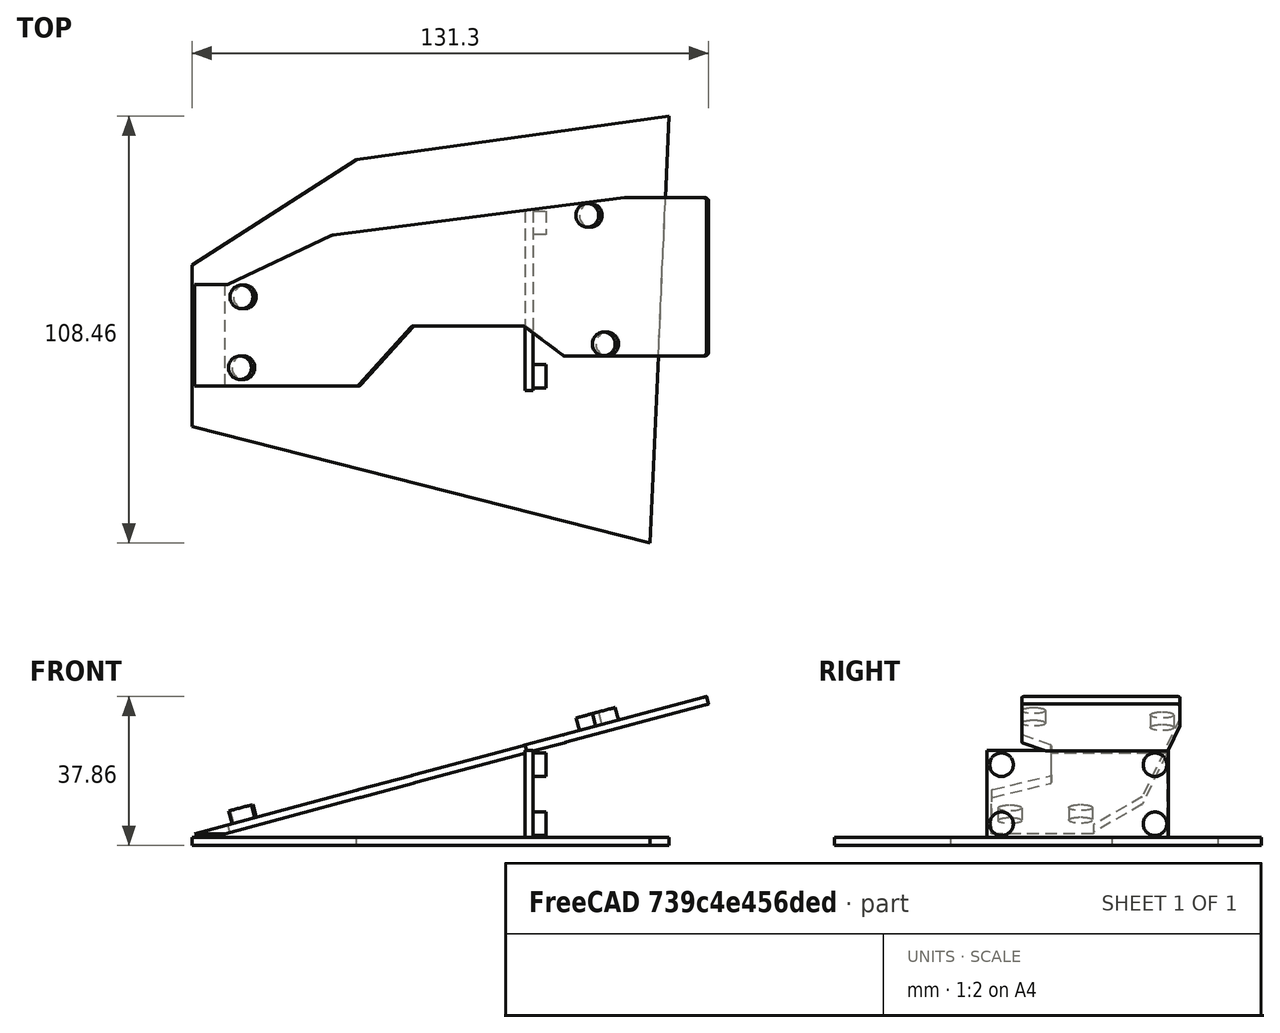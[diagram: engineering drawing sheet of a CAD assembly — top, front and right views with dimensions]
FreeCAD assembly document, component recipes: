
FREECAD ASSEMBLY — COMPONENT RECIPES ("case-tent-nojoy")

This assembly document has 2 components, labeled P0..P1 below (a component is one placed body or linked part). 1 of them carries a construction recipe — the FreeCAD feature program that regenerates the part from scratch, quoted from this document or its linked companion documents; the rest are supplied as boundary geometry only. No exploded tour is included for this assembly.
COMPONENT P0 — recipe-attached ("Part001", modeled in this document).
Construction recipe (the document's own serialized feature program — sketch geometry with constraints, then the solid features built on it; lengths are millimeters unless a unit is written):

FEATURE [PartDesign::Plane] DatumPlane  label="tilt plane"
  AttachmentOffset = pos=(0,0,0) rot=(0,-1,0;0.261799rad)
  AttachmentSupport = -> [XY_Plane001]
  Length = 193.679
  MapMode = 5
  Placement = pos=(0,0,0) rot=(0,-1,0;0.261799rad)
  ResizeMode = 0
  Width = 135.367
FEATURE [Sketcher::SketchObject] PCB_Sketch_f9e006  label="left"
  ArcFitTolerance = 1e-06
  AttachmentOffset = pos=(0,3,4.4) rot=(0,0,1;0rad)
  AttachmentSupport = -> [DatumPlane]
  FullyConstrained = false
  MakeInternals = false
  MapMode = 5
  Placement = pos=(-1.1388,3,4.25007) rot=(0,-1,0;0.261799rad)
  sketch-geometry (22):
    g0: LineSegment StartX=48.9342 StartY=15.25 StartZ=0 EndX=77.5946 EndY=15.25 EndZ=0
    g1: LineSegment StartX=27.2503 StartY=38.2054 StartZ=0 EndX=0.008196 EndY=25.8215 EndZ=0
    g2: LineSegment StartX=126 StartY=8.65 StartZ=0 EndX=126 EndY=45.95 EndZ=0
    g3: LineSegment StartX=104.439 StartY=47.8424 StartZ=0 EndX=27.5489 EndY=38.289 EndZ=0
    g4: LineSegment StartX=34.5465 StartY=0.317255 StartZ=0 EndX=48.2035 EndY=14.9327 EndZ=0
    g5: LineSegment StartX=104.562 StartY=47.85 StartZ=0 EndX=125 EndY=47.85 EndZ=0
    g6: LineSegment StartX=125 StartY=7.65 StartZ=0 EndX=88.6266 EndY=7.65 EndZ=0
    g7: LineSegment StartX=0.008196 StartY=0 StartZ=0 EndX=33.8158 EndY=-1.6e-15 EndZ=0
    g8: LineSegment StartX=126 StartY=45.95 StartZ=0 EndX=126 EndY=46.85 EndZ=0
    g9: LineSegment StartX=78.291 StartY=14.9676 StartZ=0 EndX=88.0364 EndY=7.84274 EndZ=0
    g10: ArcOfCircle CenterX=27.666 CenterY=37.2959 CenterZ=0 NormalX=0 NormalY=0 NormalZ=-1 AngleXU=1.14211 Radius=1.00001 StartAngle=0 EndAngle=0.311303
    g11: ArcOfCircle CenterX=33.8158 CenterY=1.00002 CenterZ=0 NormalX=0 NormalY=0 NormalZ=-1 AngleXU=-2.39007 Radius=1.00002 StartAngle=0 EndAngle=0.81927
    g12: ArcOfCircle CenterX=48.9342 CenterY=14.25 CenterZ=0 NormalX=0 NormalY=0 NormalZ=-1 AngleXU=0.75152 Radius=1.00002 StartAngle=0 EndAngle=0.81927
    g13: ArcOfCircle CenterX=125 CenterY=46.85 CenterZ=0 NormalX=0 NormalY=0 NormalZ=-1 AngleXU=1.5708 Radius=0.999999 StartAngle=0 EndAngle=1.5708
    g14: ArcOfCircle CenterX=125 CenterY=8.65 CenterZ=0 NormalX=0 NormalY=0 NormalZ=-1 AngleXU=3.14159 Radius=0.999999 StartAngle=0 EndAngle=1.5708
    g15: ArcOfCircle CenterX=88.6266 CenterY=8.65 CenterZ=0 NormalX=0 NormalY=0 NormalZ=-1 AngleXU=-1.57079 Radius=1 StartAngle=0 EndAngle=0.631296
    g16: ArcOfCircle CenterX=104.562 CenterY=46.8498 CenterZ=0 NormalX=0 NormalY=0 NormalZ=-1 AngleXU=1.44719 Radius=1.00016 StartAngle=0 EndAngle=0.123594
    g17: ArcOfCircle CenterX=77.5946 CenterY=14.25 CenterZ=0 NormalX=0 NormalY=0 NormalZ=-1 AngleXU=1.57078 Radius=0.999961 StartAngle=0 EndAngle=0.770416
    g18: GeomPoint [constr] X=4.15 Y=4.65 Z=0
    g19: GeomPoint [constr] X=95.5 Y=43.35 Z=0
    g20: GeomPoint [constr] X=99.8333 Y=10.6833 Z=0
    g21: LineSegment StartX=0.008196 StartY=25.8215 StartZ=0 EndX=0.008196 EndY=0 EndZ=0
  constraints (20):
    c: Coincident(g1,g10)
    c: Coincident(g3,g10)
    c: Coincident(g7,g11)
    c: Coincident(g4,g11)
    c: Coincident(g4,g12)
    c: Coincident(g0,g12)
    c: Coincident(g0,g17)
    c: Coincident(g9,g17)
    c: Coincident(g9,g15)
    c: Coincident(g6,g15)
    c: Coincident(g3,g16)
    c: Coincident(g5,g16)
    c: Coincident(g6,g14)
    c: Coincident(g5,g13)
    c: Coincident(g2,g14)
    c: Coincident(g2,g8)
    c: Coincident(g8,g13)
    c: Coincident(g1,g21)
    c: Coincident(g21,g7)
    c: Vertical(g21)
FEATURE [PartDesign::Pad] Pad
  Direction = (-0.258819,0,0.965926)
  Length = 2
  Length2 = 10
  Placement = pos=(0,0,0) rot=(0,-1,0;0.261799rad)
  Profile = -> PCB_Sketch_f9e006
  ReferenceAxis = -> PCB_Sketch_f9e006 [N_Axis]
  Refine = true
  Reversed = true
  Suppressed = false
  Type = 0
FEATURE [PartDesign::Plane] DatumPlane001
  AttachmentOffset = pos=(0,0,2) rot=(0,0,1;0rad)
  AttachmentSupport = -> [XY_Plane001]
  Length = 180.277
  MapMode = 5
  Placement = pos=(0,0,2) rot=(0,0,1;0rad)
  ResizeMode = 0
  Width = 134.349
FEATURE [Sketcher::SketchObject] Sketch001
  ArcFitTolerance = 1e-06
  AttacherType = Attacher::AttachEngine3D
  AttachmentSupport = -> [Pad]
  FullyConstrained = false
  MakeInternals = false
  MapMode = 5
  Placement = pos=(0.00791673,0,0.00212128) rot=(0.621515,-0.621515,-0.476905;2.25159rad)
  sketch-geometry (4):
    g0: LineSegment StartX=-28.8215 StartY=4.4 StartZ=0 EndX=-28.8215 EndY=2.4 EndZ=0
    g1: LineSegment StartX=-28.8215 StartY=2.4 StartZ=0 EndX=-3 EndY=2.4 EndZ=0
    g2: LineSegment StartX=-3 StartY=2.4 StartZ=0 EndX=-3 EndY=4.4 EndZ=0
    g3: LineSegment StartX=-3 StartY=4.4 StartZ=0 EndX=-28.8215 EndY=4.4 EndZ=0
  constraints (8):
    c: Coincident(g0,g1)
    c: Coincident(g1,g2)
    c: Coincident(g2,g3)
    c: Coincident(g3,g0)
    c: Vertical(g0)
    c: Vertical(g2)
    c: Horizontal(g1)
    c: Horizontal(g3)
FEATURE [Sketcher::SketchObject] Sketch
  ArcFitTolerance = 1e-06
  AttachmentSupport = -> [XY_Plane001]
  FullyConstrained = false
  MakeInternals = false
  MapMode = 5
  sketch-geometry (5):
    g0: LineSegment StartX=-10.2101 StartY=33.6647 StartZ=0 EndX=-10.2101 EndY=-7.34119 EndZ=0
    g1: LineSegment StartX=-10.2101 StartY=-7.34119 StartZ=0 EndX=106.194 EndY=-36.883 EndZ=0
    g2: LineSegment StartX=106.194 StartY=-36.883 StartZ=0 EndX=111.044 EndY=71.5841 EndZ=0
    g3: LineSegment StartX=111.044 StartY=71.5841 StartZ=0 EndX=31.6776 EndY=60.561 EndZ=0
    g4: LineSegment StartX=31.6776 StartY=60.561 StartZ=0 EndX=-10.2101 EndY=33.6647 EndZ=0
  constraints (6):
    c: Vertical(g0)
    c: Coincident(g0,g1)
    c: Coincident(g1,g2)
    c: Coincident(g2,g3)
    c: Coincident(g3,g4)
    c: Coincident(g4,g0)
FEATURE [PartDesign::Pad] Pad003
  BaseFeature = -> Pad
  Direction = (0,0,1)
  Length = 2
  Length2 = 10
  Midplane = true
  Placement = pos=(0,0,0) rot=(0,-1,0;0.261799rad)
  Profile = -> Sketch
  ReferenceAxis = -> Sketch [N_Axis]
  Refine = true
  Suppressed = false
  Type = 0
FEATURE [Sketcher::SketchObject] Sketch002
  ArcFitTolerance = 1e-06
  AttachmentSupport = -> [XY_Plane001]
  ExternalGeometry = -> [PCB_Sketch_f9e006]
  FullyConstrained = false
  MakeInternals = false
  MapMode = 5
  sketch-geometry (5):
    g0: LineSegment StartX=74.4845 StartY=17.9676 StartZ=0 EndX=74.4845 EndY=1.83853 EndZ=0
    g1: LineSegment StartX=74.4845 StartY=1.83853 StartZ=0 EndX=76.4845 EndY=1.83853 EndZ=0
    g2: LineSegment StartX=76.4845 StartY=1.83853 StartZ=0 EndX=76.4845 EndY=47.8508 EndZ=0
    g3: LineSegment StartX=76.4845 StartY=47.8508 StartZ=0 EndX=74.4845 EndY=47.5936 EndZ=0
    g4: LineSegment StartX=74.4845 StartY=47.5936 StartZ=0 EndX=74.4845 EndY=17.9676 EndZ=0
  constraints (13):
    c: Coincident(g-3,g0)
    c: Vertical(g0)
    c: Coincident(g0,g1)
    c: Horizontal(g1)
    c: Coincident(g1,g2)
    c: PointOnObject(g2,g-4)
    c: Vertical(g2)
    c: Coincident(g2,g3)
    c: PointOnObject(g3,g-4)
    c: Coincident(g3,g4)
    c: Coincident(g4,g0)
    c: Vertical(g4)
    c: DistanceX(g1,g1) = 2
FEATURE [PartDesign::Pad] Pad004
  BaseFeature = -> Pad003
  Direction = (0,0,1)
  Length = 23.1
  Length2 = 10
  Placement = pos=(0,0,0) rot=(0,-1,0;0.261799rad)
  Profile = -> Sketch002
  ReferenceAxis = -> Sketch002 [N_Axis]
  Refine = true
  Suppressed = false
  Type = 0
FEATURE [Sketcher::SketchObject] PCB_Sketch_58ce  label="thumb cluster"
  ArcFitTolerance = 1e-06
  AttachmentOffset = pos=(2.5,22.5,0) rot=(0,0,1;-1.5708rad)
  AttachmentSupport = -> [Pad004]
  FullyConstrained = false
  MakeInternals = false
  MapMode = 5
  Placement = pos=(76.4845,2.5,22.5) rot=(0,-1,0;4.71239rad)
  sketch-geometry (16):
    g0: LineSegment StartX=21 StartY=44 StartZ=0 EndX=21 EndY=1 EndZ=0
    g1: LineSegment StartX=20 StartY=1e-16 StartZ=0 EndX=1 EndY=0 EndZ=0
    g2: LineSegment StartX=1 StartY=45 StartZ=0 EndX=20 EndY=45 EndZ=0
    g3: LineSegment StartX=1e-16 StartY=1 StartZ=0 EndX=3.3e-15 EndY=44 EndZ=0
    g4: ArcOfCircle CenterX=20 CenterY=44 CenterZ=0 NormalX=0 NormalY=0 NormalZ=-1 AngleXU=1.5708 Radius=0.999999 StartAngle=0 EndAngle=1.5708
    g5: ArcOfCircle CenterX=0.999999 CenterY=0.999999 CenterZ=0 NormalX=0 NormalY=0 NormalZ=-1 AngleXU=-1.5708 Radius=0.999999 StartAngle=0 EndAngle=1.5708
    g6: ArcOfCircle CenterX=20 CenterY=0.999999 CenterZ=0 NormalX=0 NormalY=0 NormalZ=-1 AngleXU=3.14159 Radius=0.999999 StartAngle=0 EndAngle=1.5708
    g7: ArcOfCircle CenterX=0.999999 CenterY=44 CenterZ=0 NormalX=0 NormalY=0 NormalZ=-1 AngleXU=-7.47076e-07 Radius=0.999999 StartAngle=0 EndAngle=1.5708
    g8: GeomPoint [constr] X=3 Y=42 Z=0
    g9: GeomPoint [constr] X=18 Y=42 Z=0
    g10: GeomPoint [constr] X=18 Y=3 Z=0
    g11: GeomPoint [constr] X=3 Y=3 Z=0
    g12: Circle CenterX=3 CenterY=42 CenterZ=0 NormalX=0 NormalY=0 NormalZ=1 AngleXU=0 Radius=3
    g13: Circle CenterX=18 CenterY=42 CenterZ=0 NormalX=0 NormalY=0 NormalZ=1 AngleXU=0 Radius=3
    g14: Circle CenterX=18 CenterY=3 CenterZ=0 NormalX=0 NormalY=0 NormalZ=1 AngleXU=0 Radius=3
    g15: Circle CenterX=3 CenterY=3 CenterZ=0 NormalX=0 NormalY=0 NormalZ=1 AngleXU=0 Radius=3
  constraints (18):
    c: Coincident(g3,g5)
    c: Coincident(g3,g7)
    c: Coincident(g1,g5)
    c: Coincident(g2,g7)
    c: Coincident(g1,g6)
    c: Coincident(g2,g4)
    c: Coincident(g0,g6)
    c: Coincident(g0,g4)
    c: Diameter(g12) = 6
    c: Coincident(g12,g8)
    c: Diameter(g13) = 6
    c: Coincident(g13,g9)
    c: Tangent(g13,g0)
    c: Diameter(g14) = 6
    c: Coincident(g14,g10)
    c: Tangent(g14,g0)
    c: Diameter(g15) = 6
    c: Coincident(g15,g11)
FEATURE [Sketcher::SketchObject] Sketch004
  ArcFitTolerance = 1e-06
  AttacherType = Attacher::AttachEngine3D
  AttachmentSupport = -> [Pad004]
  ExternalGeometry = -> [PCB_Sketch_58ce]
  FullyConstrained = true
  MakeInternals = false
  MapMode = 5
  Placement = pos=(76.4845,0,-4.2e-15) rot=(0.57735,0.57735,0.57735;2.0944rad)
  sketch-geometry (4):
    g0: Circle CenterX=5.5 CenterY=19.5 CenterZ=0 NormalX=0 NormalY=0 NormalZ=1 AngleXU=0 Radius=3
    g1: Circle CenterX=44.5 CenterY=19.5 CenterZ=0 NormalX=0 NormalY=0 NormalZ=1 AngleXU=0 Radius=3
    g2: Circle CenterX=44.5 CenterY=4.5 CenterZ=0 NormalX=0 NormalY=0 NormalZ=1 AngleXU=0 Radius=3
    g3: Circle CenterX=5.5 CenterY=4.5 CenterZ=0 NormalX=0 NormalY=0 NormalZ=1 AngleXU=0 Radius=3
  constraints (8):
    c: Coincident(g0,g-3)
    c: Equal(g0,g-3)
    c: Coincident(g1,g-4)
    c: Equal(g1,g-4)
    c: Coincident(g2,g-5)
    c: Equal(g2,g-5)
    c: Coincident(g3,g-6)
    c: Equal(g3,g-6)
FEATURE [PartDesign::Pad] Pad006
  BaseFeature = -> Pad004
  Direction = (1,0,0)
  Length = 3.3
  Length2 = 10
  Placement = pos=(0,0,0) rot=(0,-1,0;0.261799rad)
  Profile = -> Sketch004
  ReferenceAxis = -> Sketch004 [N_Axis]
  Refine = true
  Suppressed = false
  Type = 0
FEATURE [PartDesign::Pad] Pad007
  BaseFeature = -> Pad006
  Direction = (-0.965926,-1e-16,-0.258819)
  Length = 10
  Length2 = 10
  Placement = pos=(0,0,0) rot=(0,-1,0;0.261799rad)
  Profile = -> Sketch001
  ReferenceAxis = -> Sketch001 [N_Axis]
  Refine = true
  Suppressed = false
  Type = 3
  UpToFace = -> DatumPlane001
FEATURE [Sketcher::SketchObject] Sketch005
  ArcFitTolerance = 1e-06
  AttachmentSupport = -> [Pad007]
  FullyConstrained = false
  MakeInternals = false
  MapMode = 5
  Placement = pos=(-1.1388,-1e-16,4.25007) rot=(0,-1,0;0.261799rad)
  sketch-geometry (4):
    g0: Circle CenterX=95.5 CenterY=46.35 CenterZ=0 NormalX=0 NormalY=0 NormalZ=1 AngleXU=0 Radius=3
    g1: Circle CenterX=99.8333 CenterY=13.6833 CenterZ=0 NormalX=0 NormalY=0 NormalZ=1 AngleXU=0 Radius=3
    g2: Circle CenterX=4.5434 CenterY=25.6249 CenterZ=0 NormalX=0 NormalY=0 NormalZ=1 AngleXU=0 Radius=3
    g3: Circle CenterX=4.15 CenterY=7.65 CenterZ=0 NormalX=0 NormalY=0 NormalZ=1 AngleXU=0 Radius=3
  constraints (4):
    c: Diameter(g0) = 6
    c: Diameter(g1) = 6
    c: Diameter(g2) = 6
    c: Diameter(g3) = 6
FEATURE [PartDesign::Pad] Pad008
  BaseFeature = -> Pad007
  Direction = (-0.258819,0,0.965926)
  Length = 3.3
  Length2 = 10
  Placement = pos=(0,0,0) rot=(0,-1,0;0.261799rad)
  Profile = -> Sketch005
  ReferenceAxis = -> Sketch005 [N_Axis]
  Refine = true
  Suppressed = false
  Type = 0
FEATURE [PartDesign::Body] Body
  AllowCompound = true
  Group = -> [DatumPlane,PCB_Sketch_f9e006,Pad,PCB_Sketch_58ce,DatumPlane001,Sketch001,Sketch,Pad003,Sketch002,Pad004,Sketch004,Pad006,Pad007,Sketch005,Pad008]
  Origin = -> Origin001
  Tip = -> Pad008
COMPONENT P1 — geometry summary ("left001"; no construction recipe available for this part):
  bounding box: 122.4 x 48.0 x 38.4 mm
  tessellated surface: 118,062 triangles
  volume: 8489 mm^3 (4% of its bounding box)
PROVENANCE & LICENSES
A FreeCAD (.FCStd) document from a public repository crawl; recipes are the document's own serialized feature recipes (and, for linked parts, companion documents' recipes).
License: gpl-3.0.
